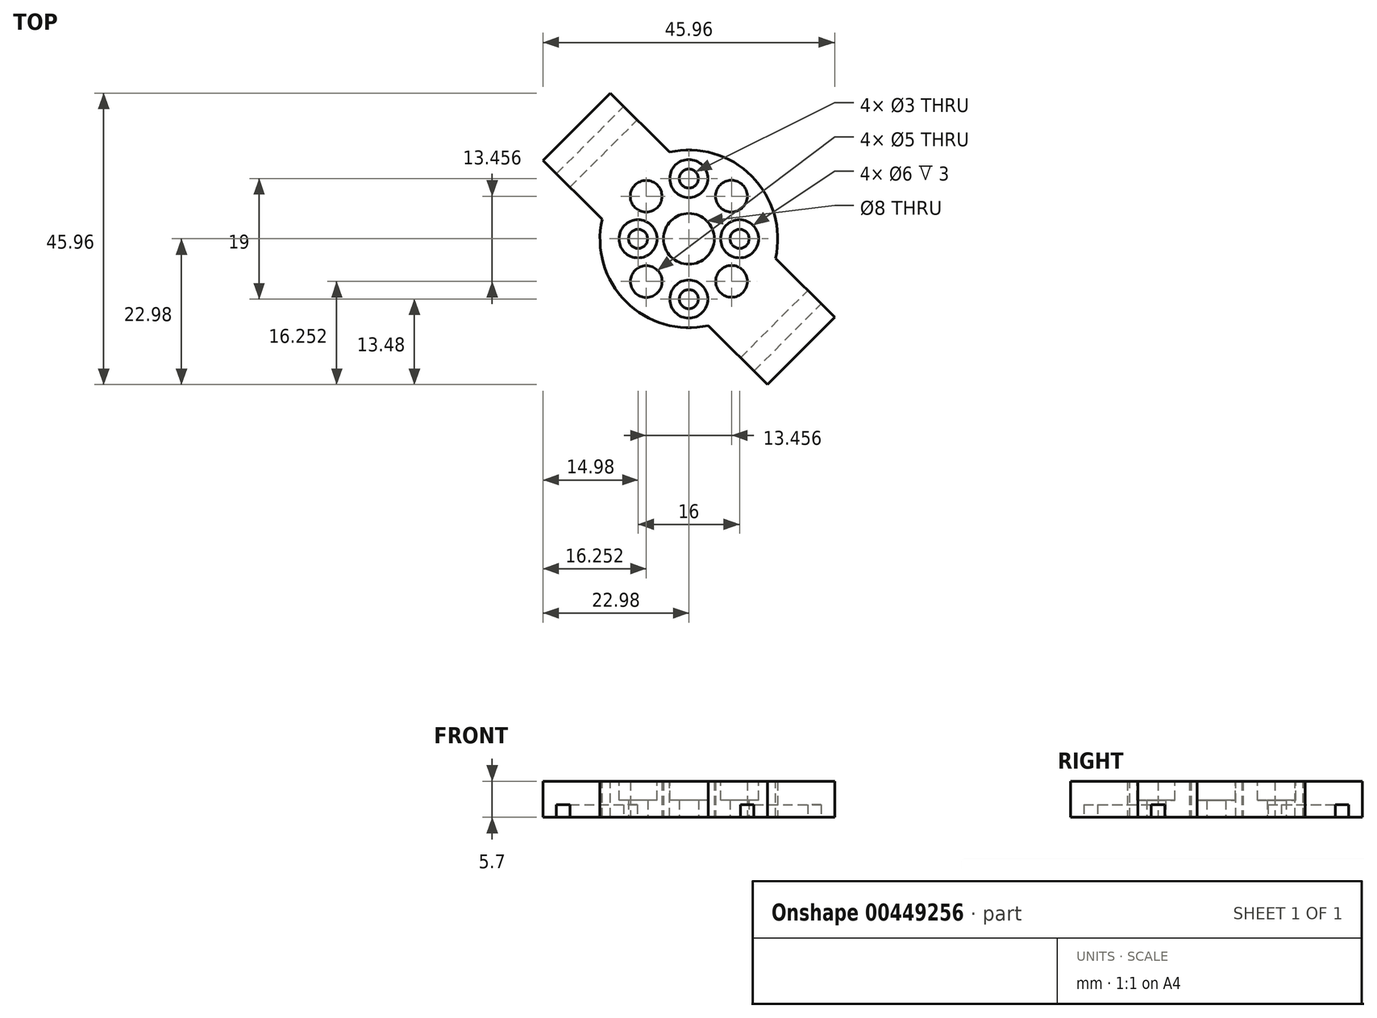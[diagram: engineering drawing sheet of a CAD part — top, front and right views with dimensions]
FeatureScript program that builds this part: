
annotation { "Feature Type Name" : "Feature", "Feature Type Description" : "" }
export const myFeature = defineFeature(function(context is Context, id is Id, definition is map)
    precondition{}
    {
        {
            var Q0;
            Q0=qCreatedBy(makeId("Top.planeOp"),FACE);
            var sketch = newSketch(context, id + "F0", { "sketchPlane" : qUnion([Q0])});
            skCircle(sketch, "E0", {"center": v(0, 0) * mm, "radius": 14 * mm});
            skCircle(sketch, "E1", {"center": v(0, 0) * mm, "radius": 9.5 * mm, "construction": true});
            skCircle(sketch, "E2", {"center": v(0, 0) * mm, "radius": 8 * mm, "construction": true});
            skCircle(sketch, "E3", {"center": v(0, 9.5) * mm, "radius": 1.5 * mm});
            skCircle(sketch, "E4", {"center": v(-8, 0) * mm, "radius": 1.5 * mm});
            skCircle(sketch, "E5.MirrorC", {"center": v(8, 0) * mm, "radius": 1.5 * mm});
            skCircle(sketch, "E6.MirrorC", {"center": v(0, -9.5) * mm, "radius": 1.5 * mm});
            skCircle(sketch, "E7", {"center": v(-6.73, 6.7) * mm, "radius": 2.5 * mm});
            skCircle(sketch, "E8.1.0", {"center": v(-6.7, -6.73) * mm, "radius": 2.5 * mm});
            skCircle(sketch, "E8.2.0", {"center": v(6.73, -6.7) * mm, "radius": 2.5 * mm});
            skCircle(sketch, "E8.3.0", {"center": v(6.7, 6.73) * mm, "radius": 2.5 * mm});
            skCircle(sketch, "E9", {"center": v(0, 0) * mm, "radius": 4 * mm});
            skLineSegment(sketch, "E10", {"start": v(0, 0) * mm, "end": v(6.7, 6.73) * mm, "construction": true});
            skLineSegment(sketch, "E11", {"start": v(0, 0) * mm, "end": v(6.73, -6.7) * mm, "construction": true});
            skSolve(sketch);
        }
        {
            var Q0;
            Q0=makeQuery(id+"F0.imprint","IMPRINT",FACE,{"disambiguationData":[TD([[makeQuery(id+"F0.imprint","IMPRINT",EDGE,{"derivedFrom":sQuery(id+"F0.wireOp",EDGE,"E0")}),1.0]])]});
            extrude(context, id + "F1", {"entities" : qUnion([Q0]), "depth" : 5.7 * mm});
        }
        {
            var Q0;
            Q0=makeQuery(id+"F1.opExtrude","CAP_FACE",FACE,{"disambiguationData":[OSD([sQuery(id+"F0.wireOp",EDGE,"E0"),sQuery(id+"F0.wireOp",EDGE,"E3"),sQuery(id+"F0.wireOp",EDGE,"E4"),sQuery(id+"F0.wireOp",EDGE,"E5.MirrorC"),sQuery(id+"F0.wireOp",EDGE,"E6.MirrorC"),sQuery(id+"F0.wireOp",EDGE,"E7"),sQuery(id+"F0.wireOp",EDGE,"E8.1.0"),sQuery(id+"F0.wireOp",EDGE,"E8.2.0"),sQuery(id+"F0.wireOp",EDGE,"E8.3.0"),sQuery(id+"F0.wireOp",EDGE,"E9")])],"isStart":false});
            var sketch = newSketch(context, id + "F2", { "sketchPlane" : qUnion([Q0])});
            skCircle(sketch, "E12", {"center": v(0, 9.5) * mm, "radius": 3 * mm});
            skCircle(sketch, "E13", {"center": v(8, 0) * mm, "radius": 3 * mm});
            skCircle(sketch, "E14", {"center": v(0, -9.5) * mm, "radius": 3 * mm});
            skCircle(sketch, "E15", {"center": v(-8, 0) * mm, "radius": 3 * mm});
            skSolve(sketch);
        }
        {
            var Q0;
            Q0=makeQuery(id+"F2.imprint","IMPRINT",FACE,{"disambiguationData":[TD([[makeQuery(id+"F2.imprint","IMPRINT",EDGE,{"derivedFrom":sQuery(id+"F2.wireOp",EDGE,"E12")}),1.0]])]});
            var Q1;
            Q1=makeQuery(id+"F2.imprint","IMPRINT",FACE,{"disambiguationData":[TD([[makeQuery(id+"F2.imprint","IMPRINT",EDGE,{"derivedFrom":sQuery(id+"F2.wireOp",EDGE,"E15")}),1.0]])]});
            var Q2;
            Q2=makeQuery(id+"F2.imprint","IMPRINT",FACE,{"disambiguationData":[TD([[makeQuery(id+"F2.imprint","IMPRINT",EDGE,{"derivedFrom":sQuery(id+"F2.wireOp",EDGE,"E14")}),1.0]])]});
            var Q3;
            Q3=makeQuery(id+"F2.imprint","IMPRINT",FACE,{"disambiguationData":[TD([[makeQuery(id+"F2.imprint","IMPRINT",EDGE,{"derivedFrom":sQuery(id+"F2.wireOp",EDGE,"E13")}),1.0]])]});
            extrude(context, id + "F3", {"entities" : qUnion([Q0, Q1, Q2, Q3]), "operationType" : NewBodyOperationType.REMOVE, "oppositeDirection" : true, "depth" : 3 * mm});
        }
        {
            var Q0;
            Q0=makeQuery(id+"F1.opExtrude","CAP_FACE",FACE,{"disambiguationData":[OSD([sQuery(id+"F0.wireOp",EDGE,"E0"),sQuery(id+"F0.wireOp",EDGE,"E3"),sQuery(id+"F0.wireOp",EDGE,"E4"),sQuery(id+"F0.wireOp",EDGE,"E5.MirrorC"),sQuery(id+"F0.wireOp",EDGE,"E6.MirrorC"),sQuery(id+"F0.wireOp",EDGE,"E7"),sQuery(id+"F0.wireOp",EDGE,"E8.1.0"),sQuery(id+"F0.wireOp",EDGE,"E8.2.0"),sQuery(id+"F0.wireOp",EDGE,"E8.3.0"),sQuery(id+"F0.wireOp",EDGE,"E9")])],"isStart":false});
            var sketch = newSketch(context, id + "F4", { "sketchPlane" : qUnion([Q0])});
            skLineSegment(sketch, "E16.bottom", {"start": v(22.98, -12.37) * mm, "end": v(12.37, -22.98) * mm});
            skLineSegment(sketch, "E16.top", {"start": v(-12.37, 22.98) * mm, "end": v(-22.98, 12.37) * mm});
            skLineSegment(sketch, "E16.left", {"start": v(22.98, -12.37) * mm, "end": v(-12.37, 22.98) * mm});
            skLineSegment(sketch, "E16.right", {"start": v(12.37, -22.98) * mm, "end": v(-22.98, 12.37) * mm});
            skPoint(sketch, "E16.middle", {"position": v(0, 0) * mm});
            skSolve(sketch);
        }
        {
            var Q0;
            {var subQ0=sQuery(id+"F4.wireOp",EDGE,"E16.top");Q0=makeQuery(id+"F4.imprint","IMPRINT",FACE,{"disambiguationData":[TD([[makeQuery(id+"F4.imprint","IMPRINT",EDGE,{"derivedFrom":subQ0}),1.0]])]});}
            var Q1;
            {var subQ0=sQuery(id+"F4.wireOp",EDGE,"E16.bottom");Q1=makeQuery(id+"F4.imprint","IMPRINT",FACE,{"disambiguationData":[TD([[makeQuery(id+"F4.imprint","IMPRINT",EDGE,{"derivedFrom":subQ0}),-1.0]])]});}
            extrude(context, id + "F5", {"entities" : qUnion([Q0, Q1]), "operationType" : NewBodyOperationType.ADD, "oppositeDirection" : true, "depth" : 5.7 * mm});
        }
        {
            var Q0;
            {var subQ0=sQuery(id+"F4.wireOp",EDGE,"E16.right");var subQ1=sQuery(id+"F4.wireOp",EDGE,"E16.left");var subQ2=sQuery(id+"F0.wireOp",EDGE,"E0");Q0=makeQuery(id+"F5.boolean.opBoolean","MERGE",FACE,{"derivedFrom":[makeQuery(id+"F1.opExtrude","CAP_FACE",FACE,{"disambiguationData":[OSD([subQ2,sQuery(id+"F0.wireOp",EDGE,"E3"),sQuery(id+"F0.wireOp",EDGE,"E4"),sQuery(id+"F0.wireOp",EDGE,"E5.MirrorC"),sQuery(id+"F0.wireOp",EDGE,"E6.MirrorC"),sQuery(id+"F0.wireOp",EDGE,"E7"),sQuery(id+"F0.wireOp",EDGE,"E8.1.0"),sQuery(id+"F0.wireOp",EDGE,"E8.2.0"),sQuery(id+"F0.wireOp",EDGE,"E8.3.0"),sQuery(id+"F0.wireOp",EDGE,"E9")])],"isStart":true}),makeQuery(id+"F5.opExtrude","CAP_FACE",FACE,{"disambiguationData":[OSD([subQ2,sQuery(id+"F4.wireOp",EDGE,"E16.bottom"),subQ1,subQ0])],"isStart":false}),makeQuery(id+"F5.opExtrude","CAP_FACE",FACE,{"disambiguationData":[OSD([subQ2,sQuery(id+"F4.wireOp",EDGE,"E16.top"),subQ1,subQ0])],"isStart":false})]});}
            var sketch = newSketch(context, id + "F6", { "sketchPlane" : qUnion([Q0])});
            skLineSegment(sketch, "E17.bottom", {"start": v(10.25, 20.86) * mm, "end": v(20.86, 10.25) * mm});
            skLineSegment(sketch, "E17.top", {"start": v(8.13, 18.74) * mm, "end": v(18.74, 8.13) * mm});
            skLineSegment(sketch, "E17.left", {"start": v(10.25, 20.86) * mm, "end": v(8.13, 18.74) * mm});
            skLineSegment(sketch, "E17.right", {"start": v(20.86, 10.25) * mm, "end": v(18.74, 8.13) * mm});
            skLineSegment(sketch, "E18.bottom", {"start": v(-20.86, -10.25) * mm, "end": v(-10.25, -20.86) * mm});
            skLineSegment(sketch, "E18.top", {"start": v(-18.74, -8.13) * mm, "end": v(-8.13, -18.74) * mm});
            skLineSegment(sketch, "E18.left", {"start": v(-18.74, -8.13) * mm, "end": v(-20.86, -10.25) * mm});
            skLineSegment(sketch, "E18.right", {"start": v(-8.13, -18.74) * mm, "end": v(-10.25, -20.86) * mm});
            skSolve(sketch);
        }
        {
            var Q0;
            Q0=makeQuery(id+"F6.imprint","IMPRINT",FACE,{"disambiguationData":[TD([[makeQuery(id+"F6.imprint","IMPRINT",EDGE,{"derivedFrom":sQuery(id+"F6.wireOp",EDGE,"E18.bottom")}),1.0]])]});
            var Q1;
            Q1=makeQuery(id+"F6.imprint","IMPRINT",FACE,{"disambiguationData":[TD([[makeQuery(id+"F6.imprint","IMPRINT",EDGE,{"derivedFrom":sQuery(id+"F6.wireOp",EDGE,"E17.bottom")}),-1.0]])]});
            extrude(context, id + "F7", {"entities" : qUnion([Q0, Q1]), "operationType" : NewBodyOperationType.REMOVE, "oppositeDirection" : true, "depth" : 2 * mm});
        }
    });
